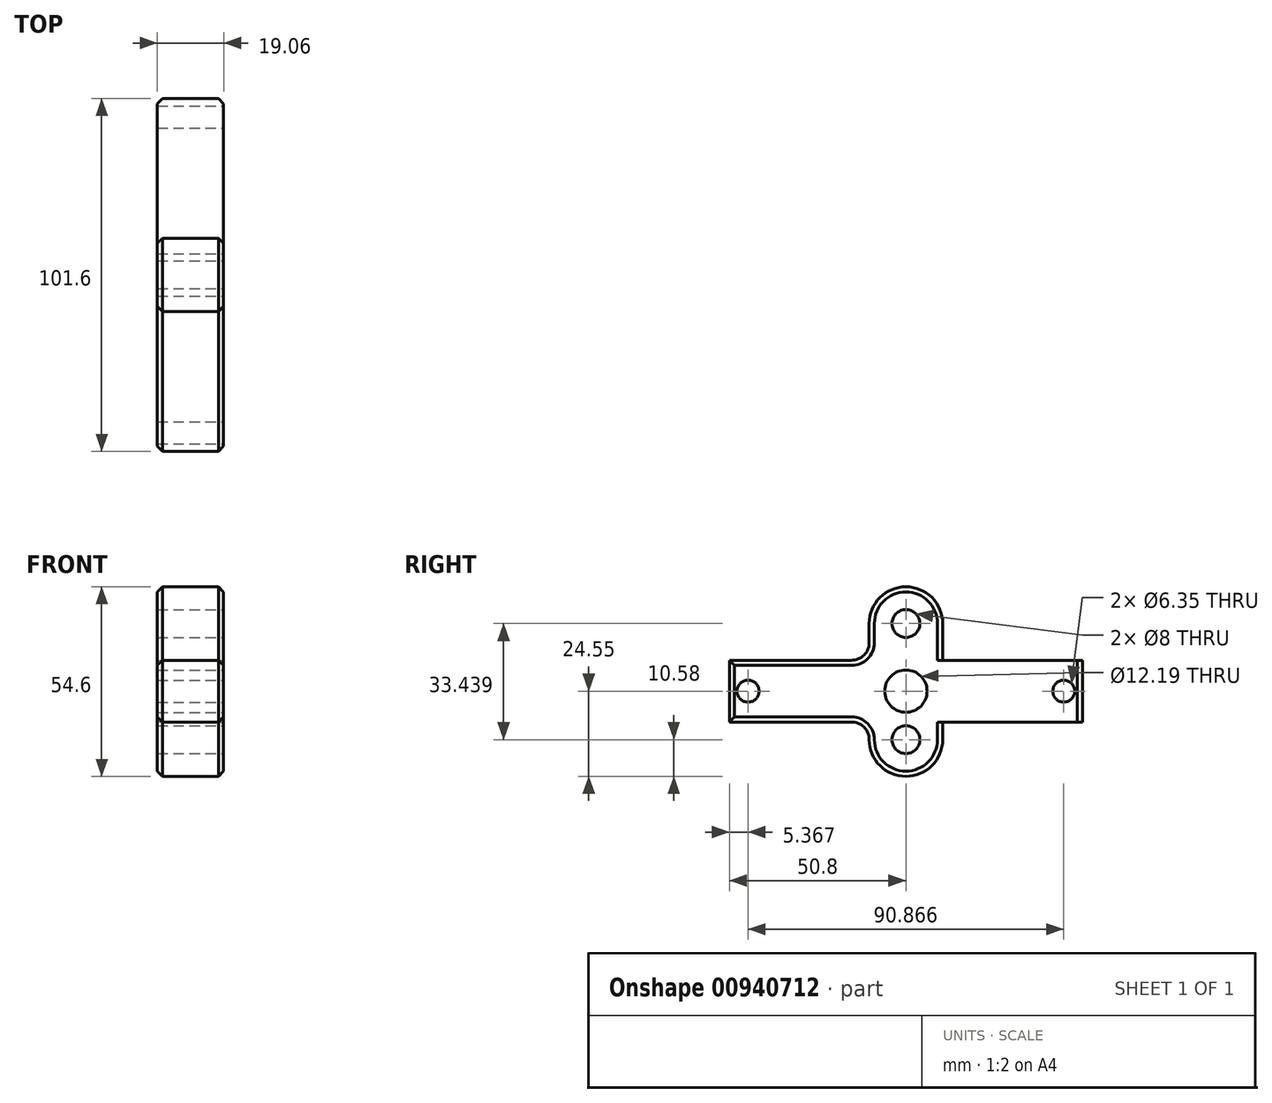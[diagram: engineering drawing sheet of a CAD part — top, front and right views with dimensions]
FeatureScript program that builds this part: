
annotation { "Feature Type Name" : "Feature", "Feature Type Description" : "" }
export const myFeature = defineFeature(function(context is Context, id is Id, definition is map)
    precondition{}
    {
        {
            var Q0;
            Q0=qCreatedBy(makeId("Front.planeOp"),FACE);
            var sketch = newSketch(context, id + "F0", { "sketchPlane" : qUnion([Q0])});
            skLineSegment(sketch, "E0.bottom", {"start": v(9.53, 8.9) * mm, "end": v(-9.53, 8.9) * mm});
            skLineSegment(sketch, "E0.top", {"start": v(9.53, -8.89) * mm, "end": v(-9.53, -8.89) * mm});
            skLineSegment(sketch, "E0.left", {"start": v(9.53, 8.9) * mm, "end": v(9.53, -8.89) * mm});
            skLineSegment(sketch, "E0.right", {"start": v(-9.53, 8.9) * mm, "end": v(-9.53, -8.89) * mm});
            skPoint(sketch, "E0.middle", {"position": v(0, 0) * mm});
            skSolve(sketch);
        }
        {
            var Q0;
            Q0 = qSketchRegion(id + "F0", true);
            extrude(context, id + "F1", {"entities" : qUnion([Q0]), "endBound" : BoundingType.SYMMETRIC, "depth" : 101.6 * mm, "offsetDistance" : 25.4 * mm});
        }
        {
            var Q0;
            Q0=makeQuery(id+"F1.opExtrude","SWEPT_FACE",FACE,{"disambiguationData":[OSD([sQuery(id+"F0.wireOp",EDGE,"E0.left")])]});
            var sketch = newSketch(context, id + "F2", { "sketchPlane" : qUnion([Q0])});
            skCircle(sketch, "E1", {"center": v(-45.43, 0) * mm, "radius": 3.18 * mm});
            skCircle(sketch, "E2", {"center": v(45.43, 0) * mm, "radius": 3.18 * mm});
            skLineSegment(sketch, "E3", {"start": v(-45.43, 0) * mm, "end": v(45.43, 0) * mm, "construction": true});
            skCircle(sketch, "E4", {"center": v(0, 0) * mm, "radius": 6.1 * mm});
            skSolve(sketch);
        }
        {
            var Q0;
            Q0 = qSketchRegion(id + "F2", true);
            extrude(context, id + "F3", {"entities" : qUnion([Q0]), "operationType" : NewBodyOperationType.REMOVE, "endBound" : BoundingType.THROUGH_ALL, "oppositeDirection" : true, "depth" : 25.4 * mm, "offsetDistance" : 25.4 * mm});
        }
        {
            var Q0;
            Q0=makeQuery(id+"F1.opExtrude","SWEPT_FACE",FACE,{"disambiguationData":[OSD([sQuery(id+"F0.wireOp",EDGE,"E0.left")])]});
            var sketch = newSketch(context, id + "F4", { "sketchPlane" : qUnion([Q0])});
            skCircle(sketch, "E5", {"center": v(0, 19.47) * mm, "radius": 4 * mm});
            skLineSegment(sketch, "E6", {"start": v(0, 19.47) * mm, "end": v(0, 0) * mm, "construction": true});
            skLineSegment(sketch, "E7", {"start": v(-10.58, 8.9) * mm, "end": v(-10.58, 19.47) * mm});
            skLineSegment(sketch, "E8", {"start": v(10.58, 19.47) * mm, "end": v(10.58, 8.9) * mm});
            skLineSegment(sketch, "E9", {"start": v(10.58, 8.9) * mm, "end": v(-10.58, 8.9) * mm});
            skArc(sketch, "E10", {"start": v(10.58, 19.47) * mm, "mid": v(0, 30.05) * mm, "end": v(-10.58, 19.47) * mm});
            skCircle(sketch, "E11", {"center": v(0, -13.97) * mm, "radius": 4 * mm});
            skLineSegment(sketch, "E12", {"start": v(0, 0) * mm, "end": v(0, -13.97) * mm, "construction": true});
            skArc(sketch, "E13", {"start": v(-10.58, -13.97) * mm, "mid": v(0, -24.55) * mm, "end": v(10.58, -13.97) * mm});
            skLineSegment(sketch, "E14", {"start": v(-10.58, -8.9) * mm, "end": v(-10.58, -13.97) * mm});
            skLineSegment(sketch, "E15", {"start": v(10.58, -13.97) * mm, "end": v(10.58, -8.9) * mm});
            skLineSegment(sketch, "E16", {"start": v(10.58, -8.89) * mm, "end": v(-10.58, -8.89) * mm});
            skSolve(sketch);
        }
        {
            var Q0;
            Q0 = qSketchRegion(id + "F4", true);
            var Q1;
            Q1=makeQuery(id+"F1.opExtrude","SWEPT_FACE",FACE,{"disambiguationData":[OSD([sQuery(id+"F0.wireOp",EDGE,"E0.right")])]});
            extrude(context, id + "F5", {"entities" : qUnion([Q0]), "operationType" : NewBodyOperationType.ADD, "endBound" : BoundingType.UP_TO_SURFACE, "oppositeDirection" : true, "depth" : 25.4 * mm, "endBoundEntityFace" : qUnion([Q1]), "offsetDistance" : 25.4 * mm});
        }
        {
            var Q0;
            Q0=makeQuery(id+"F5.opExtrude","SWEPT_EDGE",EDGE,{"disambiguationData":[OSD([sQuery(id+"F0.wireOp",EDGE,"E0.bottom"),sQuery(id+"F0.wireOp",EDGE,"E0.left"),sQuery(id+"F4.wireOp",EDGE,"E7"),sQuery(id+"F4.wireOp",EDGE,"E9")])]});
            var Q1;
            Q1=makeQuery(id+"F5.opExtrude","SWEPT_EDGE",EDGE,{"disambiguationData":[OSD([sQuery(id+"F0.wireOp",EDGE,"E0.bottom"),sQuery(id+"F0.wireOp",EDGE,"E0.left"),sQuery(id+"F4.wireOp",EDGE,"E8"),sQuery(id+"F4.wireOp",EDGE,"E9")])]});
            var Q2;
            Q2=makeQuery(id+"F5.opExtrude","SWEPT_EDGE",EDGE,{"disambiguationData":[OSD([sQuery(id+"F0.wireOp",EDGE,"E0.top"),sQuery(id+"F0.wireOp",EDGE,"E0.left"),sQuery(id+"F4.wireOp",EDGE,"E14"),sQuery(id+"F4.wireOp",EDGE,"E16")])]});
            var Q3;
            Q3=makeQuery(id+"F5.opExtrude","SWEPT_EDGE",EDGE,{"disambiguationData":[OSD([sQuery(id+"F0.wireOp",EDGE,"E0.top"),sQuery(id+"F0.wireOp",EDGE,"E0.left"),sQuery(id+"F4.wireOp",EDGE,"E15"),sQuery(id+"F4.wireOp",EDGE,"E16")])]});
            fillet(context, id + "F6", {"entities" : qUnion([Q0, Q1, Q2, Q3]), "radius" : 5.08 * mm, "tangentPropagation" : true, "allowEdgeOverflow" : false});
        }
        {
            var Q0;
            {var subQ0=sQuery(id+"F4.wireOp",EDGE,"E7");var subQ1=sQuery(id+"F0.wireOp",EDGE,"E0.left");var subQ2=sQuery(id+"F0.wireOp",EDGE,"E0.bottom");Q0=makeQuery(id+"F5.boolean.opBoolean","SPLIT",EDGE,{"disambiguationData":[TD([makeQuery(id+"F5.opExtrude","SWEPT_FACE",FACE,{"disambiguationData":[OSD([subQ0])]})])],"derivedFrom":makeQuery(id+"F1.opExtrude","SWEPT_EDGE",EDGE,{"disambiguationData":[OSD([subQ2,subQ1])]})});}
            var Q1;
            {var subQ0=sQuery(id+"F0.wireOp",EDGE,"E0.left");var subQ1=sQuery(id+"F0.wireOp",EDGE,"E0.top");var subQ2=sQuery(id+"F4.wireOp",EDGE,"E14");Q1=makeQuery(id+"F5.boolean.opBoolean","SPLIT",EDGE,{"disambiguationData":[TD([makeQuery(id+"F5.opExtrude","SWEPT_FACE",FACE,{"disambiguationData":[OSD([subQ2])]})])],"derivedFrom":makeQuery(id+"F1.opExtrude","SWEPT_EDGE",EDGE,{"disambiguationData":[OSD([subQ1,subQ0])]})});}
            var Q2;
            {var subQ0=sQuery(id+"F4.wireOp",EDGE,"E7");var subQ1=sQuery(id+"F0.wireOp",EDGE,"E0.right");var subQ2=sQuery(id+"F0.wireOp",EDGE,"E0.bottom");Q2=makeQuery(id+"F5.boolean.opBoolean","SPLIT",EDGE,{"disambiguationData":[TD([makeQuery(id+"F5.opExtrude","SWEPT_FACE",FACE,{"disambiguationData":[OSD([subQ0])]})])],"derivedFrom":makeQuery(id+"F1.opExtrude","SWEPT_EDGE",EDGE,{"disambiguationData":[OSD([subQ2,subQ1])]})});}
            var Q3;
            {var subQ0=sQuery(id+"F0.wireOp",EDGE,"E0.right");var subQ1=sQuery(id+"F0.wireOp",EDGE,"E0.top");var subQ2=sQuery(id+"F4.wireOp",EDGE,"E14");Q3=makeQuery(id+"F5.boolean.opBoolean","SPLIT",EDGE,{"disambiguationData":[TD([makeQuery(id+"F5.opExtrude","SWEPT_FACE",FACE,{"disambiguationData":[OSD([subQ2])]})])],"derivedFrom":makeQuery(id+"F1.opExtrude","SWEPT_EDGE",EDGE,{"disambiguationData":[OSD([subQ1,subQ0])]})});}
            var Q4;
            Q4=makeQuery(id+"F1.opExtrude","CAP_EDGE",EDGE,{"disambiguationData":[OSD([sQuery(id+"F0.wireOp",EDGE,"E0.right")])],"isStart":false});
            var Q5;
            Q5=makeQuery(id+"F1.opExtrude","CAP_EDGE",EDGE,{"disambiguationData":[OSD([sQuery(id+"F0.wireOp",EDGE,"E0.right")])],"isStart":true});
            var Q6;
            Q6=makeQuery(id+"F1.opExtrude","CAP_EDGE",EDGE,{"disambiguationData":[OSD([sQuery(id+"F0.wireOp",EDGE,"E0.left")])],"isStart":false});
            var Q7;
            Q7=makeQuery(id+"F1.opExtrude","CAP_EDGE",EDGE,{"disambiguationData":[OSD([sQuery(id+"F0.wireOp",EDGE,"E0.left")])],"isStart":true});
            chamfer(context, id + "F7", {"entities" : qUnion([Q0, Q1, Q2, Q3, Q4, Q5, Q6, Q7]), "width" : 1.5 * mm, "tangentPropagation" : true});
        }
    });
